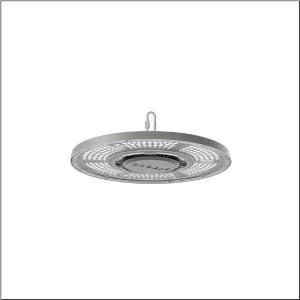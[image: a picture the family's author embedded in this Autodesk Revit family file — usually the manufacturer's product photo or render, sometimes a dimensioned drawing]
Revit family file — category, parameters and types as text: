
# Revit family: highbay_31-s_51hc417a4jmb
name_source: partatom
category: Lighting Fixtures
units: mm (PartAtom-declared; Revit-internal decimal feet)

## family parameters
Cut with Voids When Loaded = No
Host = Face
Light Source = No
Part Type = Normal
Room Calculation Point = No
Round Connector Dimension = Use Diameter
Shared = No

## types (1)
- Highbay 31-S (1 x LED, 20000 lm, 134 W, 4000K)
    Apparent Load = 134 VA
    CIE Flux Codes = 95 98 100 100 100
    Color Rendering = 80
    Color Temperature = 4000K
    Default Elevation = 1800 mm
    Description = Highbay 31-S, LED high bay luminaire, primary light control with lens, of PC, primary optical cover: cover panel, of PC, transparent, light emission: direct distribution, primary light characteristic: rotationally symmetric, installation type: suspended mounting, surface-mounted, LED, rated luminous flux: 20.000lm, luminous efficacy: 150lm/W, light colour: 840, colour temperature: 4000K, control gear: ECG, with cable, 3x 1.0mm², free wire ends, mains connection: 220..240V, AC/DC, 0/50..60Hz, cable length: 1,5m, rated input power: 134W, housing, rotationally symmetric, of diecast aluminium, powder-coated, grey aluminium (RAL 9007), with hook on luminaire side, incl. screw, diameter: 339mm, protection rating (complete): IP65, insulation class (complete): insulation class I (protective earthing), certification: CE, ENEC, UKCA, protection symbol: D, impact resistance: IK08, permissible operating ambient temperature: -30..+45°C, standard: EN 60598-2-22, EN 60598, corresponds to IFS (International Featured Standards) requirements for safety and quality in the food industry, packaging unit: 1 piece
    Height = 141 mm
    Lamp = 1 x LED
    Lamp Light Flux = 20000 lm
    Lamp Power = 134 W
    Lamp count = 1
    Length = 339 mm
    Luminous efficacy = 149 lm/W
    Manufacturer = Siteco
    ModVariant = No
    Model = 51HC417A4JMB
    Mounting Place = Ceiling
    Mounting Type = Pendant
    Number of Poles = 1
    OnlyDefault = Yes
    Power Factor = 1
    Product Name = Highbay 31-S
    Product group = LED high bay luminaire
    ProductGroupID = 903
    Protection Class = Protection class I
    Protection Degree = IP 65
    RLX_Detail_Level = 1
    RLX_Emergency_Light_Flux = 0 lm
    RLX_Emergency_Type = 0
    RLX_Emergency_Type_DB = No
    RlxData = <blob elided: 107145 chars, md5=06d9c34e>
    Socket = socket
    Standby Power = 0 W
    System Light Flux = 20000 lm
    System Power = 134 W
    Type Comments = Product without accessories
    Type Image = l_1007237.jpg
    URL = http://relux.com
    VarID = ---
    Voltage = 0 V
    Weight = 0.00 kg
    Width = 0 mm  [stored 0 ft]

note: [stored X ft] marks values corroborated as IEEE doubles in the binary element streams (Revit-internal decimal feet)

## geometry (parser evidence)
native form markers: Blend x4, Sweep x8
no freeform markers — native parametric forms only
